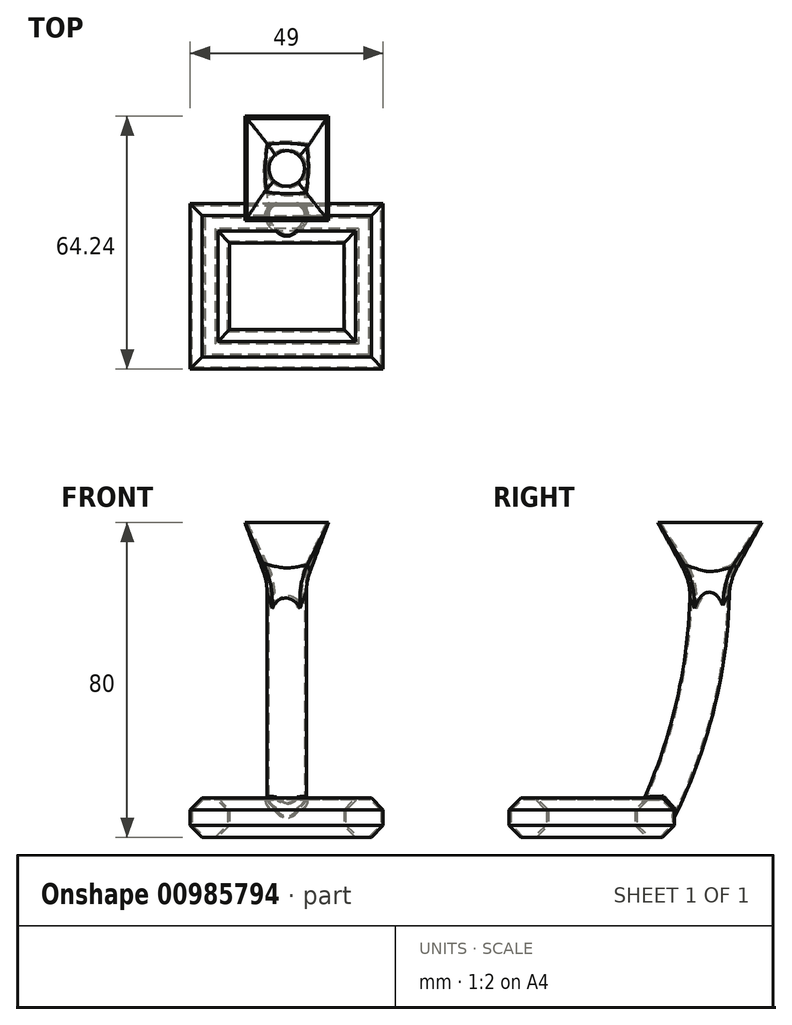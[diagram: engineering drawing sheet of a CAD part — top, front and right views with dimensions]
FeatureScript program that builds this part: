
annotation { "Feature Type Name" : "Feature", "Feature Type Description" : "" }
export const myFeature = defineFeature(function(context is Context, id is Id, definition is map)
    precondition{}
    {
        {
            assignVariable(context, id + "F0", {"variableType" : VariableType.NUMBER, "name" : "wall", "numberValue" : .5});
        }
        {
            assignVariable(context, id + "F1", {"variableType" : VariableType.LENGTH, "name" : "aird", "lengthValue" : 10 * mm});
        }
        {
            assignVariable(context, id + "F2", {"variableType" : VariableType.LENGTH, "name" : "airdr", "lengthValue" : 3 * mm});
        }
        {
            var Q0;
            Q0=qCreatedBy(makeId("Top.planeOp"),FACE);
            var sketch = newSketch(context, id + "F3", { "sketchPlane" : qUnion([Q0])});
            skLineSegment(sketch, "E0.bottom", {"start": v(11.5, 8) * mm, "end": v(-11.5, 8) * mm, "construction": true});
            skLineSegment(sketch, "E0.top", {"start": v(11.5, -8) * mm, "end": v(-11.5, -8) * mm, "construction": true});
            skLineSegment(sketch, "E0.left", {"start": v(11.5, 8) * mm, "end": v(11.5, -8) * mm, "construction": true});
            skLineSegment(sketch, "E0.right", {"start": v(-11.5, 8) * mm, "end": v(-11.5, -8) * mm, "construction": true});
            skPoint(sketch, "E0.middle", {"position": v(0, 0) * mm});
            skLineSegment(sketch, "E1.0", {"start": v(14.5, 11) * mm, "end": v(-14.5, 11) * mm});
            skLineSegment(sketch, "E1.1", {"start": v(14.5, 11) * mm, "end": v(14.5, -11) * mm});
            skLineSegment(sketch, "E1.2", {"start": v(14.5, -11) * mm, "end": v(-14.5, -11) * mm});
            skLineSegment(sketch, "E1.3", {"start": v(-14.5, 11) * mm, "end": v(-14.5, -11) * mm});
            skLineSegment(sketch, "E2.0", {"start": v(24.5, 21) * mm, "end": v(-24.5, 21) * mm});
            skLineSegment(sketch, "E2.1", {"start": v(24.5, 21) * mm, "end": v(24.5, -21) * mm});
            skLineSegment(sketch, "E2.2", {"start": v(24.5, -21) * mm, "end": v(-24.5, -21) * mm});
            skLineSegment(sketch, "E2.3", {"start": v(-24.5, 21) * mm, "end": v(-24.5, -21) * mm});
            skSolve(sketch);
        }
        {
            var Q0;
            Q0=makeQuery(id+"F3.imprint","IMPRINT",FACE,{"disambiguationData":[TD([[makeQuery(id+"F3.imprint","IMPRINT",EDGE,{"derivedFrom":sQuery(id+"F3.wireOp",EDGE,"E1.0")}),-1.0]])]});
            extrude(context, id + "F4", {"entities" : qUnion([Q0]), "depth" : getVariable(context, 'aird'), "offsetDistance" : 25 * mm});
        }
        {
            var Q0;
            Q0=makeQuery(id+"F4.opExtrude","CAP_FACE",FACE,{"disambiguationData":[OSD([sQuery(id+"F3.wireOp",EDGE,"E1.0"),sQuery(id+"F3.wireOp",EDGE,"E1.1"),sQuery(id+"F3.wireOp",EDGE,"E1.2"),sQuery(id+"F3.wireOp",EDGE,"E1.3"),sQuery(id+"F3.wireOp",EDGE,"E2.0"),sQuery(id+"F3.wireOp",EDGE,"E2.1"),sQuery(id+"F3.wireOp",EDGE,"E2.2"),sQuery(id+"F3.wireOp",EDGE,"E2.3")])],"isStart":false});
            var Q1;
            Q1=makeQuery(id+"F4.opExtrude","CAP_FACE",FACE,{"disambiguationData":[OSD([sQuery(id+"F3.wireOp",EDGE,"E1.0"),sQuery(id+"F3.wireOp",EDGE,"E1.1"),sQuery(id+"F3.wireOp",EDGE,"E1.2"),sQuery(id+"F3.wireOp",EDGE,"E1.3"),sQuery(id+"F3.wireOp",EDGE,"E2.0"),sQuery(id+"F3.wireOp",EDGE,"E2.1"),sQuery(id+"F3.wireOp",EDGE,"E2.2"),sQuery(id+"F3.wireOp",EDGE,"E2.3")])],"isStart":true});
            chamfer(context, id + "F5", {"entities" : qUnion([Q0, Q1]), "width" : getVariable(context, 'airdr'), "tangentPropagation" : true});
        }
        {
            var Q0;
            Q0=qCreatedBy(makeId("Right.planeOp"),FACE);
            var sketch = newSketch(context, id + "F6", { "sketchPlane" : qUnion([Q0])});
            skArc(sketch, "E3", {"start": v(16, 5) * mm, "mid": v(26.45, 34.2) * mm, "end": v(30, 65) * mm});
            skLineSegment(sketch, "E4", {"start": v(30, 65) * mm, "end": v(30, 55) * mm, "construction": true});
            skSolve(sketch);
        }
        {
            var Q0;
            Q0=qCreatedBy(makeId("Top.planeOp"),FACE);
            cPlane(context, id + "F7", {"entities" : qUnion([Q0]), "cplaneType" : CPlaneType.OFFSET, "offset" : 65 * mm, "width" : 150 * mm, "height" : 150 * mm});
        }
        {
            var Q0;
            Q0=qCreatedBy(id+"F7.planeOp",FACE);
            var sketch = newSketch(context, id + "F8", { "sketchPlane" : qUnion([Q0])});
            skPoint(sketch, "E5.0", {"position": v(0, 30) * mm});
            skCircle(sketch, "E6", {"center": v(0, 30) * mm, "radius": 5 * mm});
            skSolve(sketch);
        }
        {
            var Q0;
            Q0=makeQuery(id+"F8.imprint","IMPRINT",FACE,{"disambiguationData":[TD([[makeQuery(id+"F8.imprint","IMPRINT",EDGE,{"derivedFrom":sQuery(id+"F8.wireOp",EDGE,"E6")}),1.0]])]});
            var Q1;
            Q1=sQuery(id+"F6.wireOp",EDGE,"E3");
            sweep(context, id + "F9", {"operationType" : NewBodyOperationType.ADD, "profiles" : qUnion([Q0]), "path" : qUnion([Q1]), "keepProfileOrientation" : true});
        }
        {
            var Q0;
            Q0=makeQuery(id+"F9.boolean.opBoolean","INTERSECT",EDGE,{"disambiguationData":[OD(1.0)],"derivedFrom":[makeQuery(id+"F4.opExtrude","CAP_FACE",FACE,{"disambiguationData":[OSD([sQuery(id+"F3.wireOp",EDGE,"E1.0"),sQuery(id+"F3.wireOp",EDGE,"E1.1"),sQuery(id+"F3.wireOp",EDGE,"E1.2"),sQuery(id+"F3.wireOp",EDGE,"E1.3"),sQuery(id+"F3.wireOp",EDGE,"E2.0"),sQuery(id+"F3.wireOp",EDGE,"E2.1"),sQuery(id+"F3.wireOp",EDGE,"E2.2"),sQuery(id+"F3.wireOp",EDGE,"E2.3")])],"isStart":false}),makeQuery(id+"F9.opSweep","SWEPT_FACE",FACE,{"disambiguationData":[OSD([sQuery(id+"F6.wireOp",EDGE,"E3"),sQuery(id+"F8.wireOp",EDGE,"E6")])]})]});
            var Q1;
            {var subQ0=sQuery(id+"F3.wireOp",EDGE,"E1.0");Q1=makeQuery(id+"F9.boolean.opBoolean","INTERSECT",EDGE,{"derivedFrom":[makeQuery(id+"F5.opChamfer","BLEND_FACE",FACE,{"disambiguationData":[OSD([subQ0]),TDD([makeQuery(id+"F4.opExtrude","CAP_EDGE",EDGE,{"disambiguationData":[OSD([subQ0])],"isStart":false})])]}),makeQuery(id+"F9.opSweep","SWEPT_FACE",FACE,{"disambiguationData":[OSD([sQuery(id+"F6.wireOp",EDGE,"E3"),sQuery(id+"F8.wireOp",EDGE,"E6")])]})]});}
            var Q2;
            Q2=makeQuery(id+"F9.boolean.opBoolean","INTERSECT",EDGE,{"derivedFrom":[makeQuery(id+"F4.opExtrude","SWEPT_FACE",FACE,{"disambiguationData":[OSD([sQuery(id+"F3.wireOp",EDGE,"E2.0")])]}),makeQuery(id+"F9.opSweep","SWEPT_FACE",FACE,{"disambiguationData":[OSD([sQuery(id+"F6.wireOp",EDGE,"E3"),sQuery(id+"F8.wireOp",EDGE,"E6")])]})]});
            var Q3;
            {var subQ0=sQuery(id+"F3.wireOp",EDGE,"E2.0");Q3=makeQuery(id+"F9.boolean.opBoolean","INTERSECT",EDGE,{"disambiguationData":[OD(1.0)],"derivedFrom":[makeQuery(id+"F5.opChamfer","BLEND_FACE",FACE,{"disambiguationData":[OSD([subQ0]),TDD([makeQuery(id+"F4.opExtrude","CAP_EDGE",EDGE,{"disambiguationData":[OSD([subQ0])],"isStart":false})])]}),makeQuery(id+"F9.opSweep","SWEPT_FACE",FACE,{"disambiguationData":[OSD([sQuery(id+"F6.wireOp",EDGE,"E3"),sQuery(id+"F8.wireOp",EDGE,"E6")])]})]});}
            var Q4;
            Q4=makeQuery(id+"F9.boolean.opBoolean","INTERSECT",EDGE,{"disambiguationData":[OD(0.0)],"derivedFrom":[makeQuery(id+"F4.opExtrude","CAP_FACE",FACE,{"disambiguationData":[OSD([sQuery(id+"F3.wireOp",EDGE,"E1.0"),sQuery(id+"F3.wireOp",EDGE,"E1.1"),sQuery(id+"F3.wireOp",EDGE,"E1.2"),sQuery(id+"F3.wireOp",EDGE,"E1.3"),sQuery(id+"F3.wireOp",EDGE,"E2.0"),sQuery(id+"F3.wireOp",EDGE,"E2.1"),sQuery(id+"F3.wireOp",EDGE,"E2.2"),sQuery(id+"F3.wireOp",EDGE,"E2.3")])],"isStart":false}),makeQuery(id+"F9.opSweep","SWEPT_FACE",FACE,{"disambiguationData":[OSD([sQuery(id+"F6.wireOp",EDGE,"E3"),sQuery(id+"F8.wireOp",EDGE,"E6")])]})]});
            var Q5;
            {var subQ0=sQuery(id+"F3.wireOp",EDGE,"E2.0");Q5=makeQuery(id+"F9.boolean.opBoolean","INTERSECT",EDGE,{"disambiguationData":[OD(0.0)],"derivedFrom":[makeQuery(id+"F5.opChamfer","BLEND_FACE",FACE,{"disambiguationData":[OSD([subQ0]),TDD([makeQuery(id+"F4.opExtrude","CAP_EDGE",EDGE,{"disambiguationData":[OSD([subQ0])],"isStart":false})])]}),makeQuery(id+"F9.opSweep","SWEPT_FACE",FACE,{"disambiguationData":[OSD([sQuery(id+"F6.wireOp",EDGE,"E3"),sQuery(id+"F8.wireOp",EDGE,"E6")])]})]});}
            fillet(context, id + "F10", {"entities" : qUnion([Q0, Q1, Q2, Q3, Q4, Q5]), "tangentPropagation" : true, "radius" : .5 * mm, "defaultsChanged" : true, "vertexSettings" : [], "allowEdgeOverflow" : false});
        }
        {
            var Q0;
            Q0=qCreatedBy(makeId("Top.planeOp"),FACE);
            cPlane(context, id + "F11", {"entities" : qUnion([Q0]), "cplaneType" : CPlaneType.OFFSET, "offset" : 80 * mm, "width" : 150 * mm, "height" : 150 * mm});
        }
        {
            var Q0;
            Q0=qCreatedBy(id+"F11.planeOp",FACE);
            var sketch = newSketch(context, id + "F12", { "sketchPlane" : qUnion([Q0])});
            skPoint(sketch, "E7.0", {"position": v(0, 30) * mm});
            skLineSegment(sketch, "E8.bottom", {"start": v(10.63, 16.76) * mm, "end": v(-10.63, 16.76) * mm});
            skLineSegment(sketch, "E8.top", {"start": v(10.63, 43.24) * mm, "end": v(-10.63, 43.24) * mm});
            skLineSegment(sketch, "E8.left", {"start": v(10.63, 16.76) * mm, "end": v(10.63, 43.24) * mm});
            skLineSegment(sketch, "E8.right", {"start": v(-10.63, 16.76) * mm, "end": v(-10.63, 43.24) * mm});
            skSolve(sketch);
        }
        {
            var Q0;
            Q0=makeQuery(id+"F12.imprint","IMPRINT",FACE,{"disambiguationData":[TD([[makeQuery(id+"F12.imprint","IMPRINT",EDGE,{"derivedFrom":sQuery(id+"F12.wireOp",EDGE,"E8.bottom")}),-1.0]])]});
            var Q1;
            Q1=makeQuery(id+"F8.imprint","IMPRINT",FACE,{"disambiguationData":[TD([[makeQuery(id+"F8.imprint","IMPRINT",EDGE,{"derivedFrom":sQuery(id+"F8.wireOp",EDGE,"E6")}),1.0]])]});
            loft(context, id + "F13", {"operationType" : NewBodyOperationType.ADD, "sheetProfilesArray" : [{ "sheetProfileEntities" : qUnion([Q0]) }, { "sheetProfileEntities" : qUnion([Q1]) }]});
        }
        {
            var Q0;
            {var subQ0=sQuery(id+"F8.wireOp",EDGE,"E6");Q0=makeQuery(id+"F13.boolean.opBoolean","MERGE",EDGE,{"derivedFrom":[makeQuery(id+"F9.opSweep","CAP_EDGE",EDGE,{"disambiguationData":[OSD([sQuery(id+"F6.wireOp",VERTEX,"E3.end"),subQ0])],"isStart":true}),makeQuery(id+"F13.opLoft","MID_CAP_EDGE",EDGE,{"disambiguationData":[OSD([subQ0,sQuery(id+"F12.wireOp",EDGE,"E8.bottom"),sQuery(id+"F12.wireOp",EDGE,"E8.left")])],"capPos":1.0})]});}
            var Q1;
            {var subQ0=sQuery(id+"F8.wireOp",EDGE,"E6");Q1=makeQuery(id+"F13.boolean.opBoolean","MERGE",EDGE,{"derivedFrom":[makeQuery(id+"F9.opSweep","CAP_EDGE",EDGE,{"disambiguationData":[OSD([sQuery(id+"F6.wireOp",VERTEX,"E3.end"),subQ0])],"isStart":true}),makeQuery(id+"F13.opLoft","MID_CAP_EDGE",EDGE,{"disambiguationData":[OSD([subQ0,sQuery(id+"F12.wireOp",EDGE,"E8.bottom"),sQuery(id+"F12.wireOp",EDGE,"E8.left"),sQuery(id+"F12.wireOp",EDGE,"E8.right")])],"capPos":1.0})]});}
            var Q2;
            {var subQ0=sQuery(id+"F8.wireOp",EDGE,"E6");Q2=makeQuery(id+"F13.boolean.opBoolean","MERGE",EDGE,{"derivedFrom":[makeQuery(id+"F9.opSweep","CAP_EDGE",EDGE,{"disambiguationData":[OSD([sQuery(id+"F6.wireOp",VERTEX,"E3.end"),subQ0])],"isStart":true}),makeQuery(id+"F13.opLoft","MID_CAP_EDGE",EDGE,{"disambiguationData":[OSD([subQ0,sQuery(id+"F12.wireOp",EDGE,"E8.bottom"),sQuery(id+"F12.wireOp",EDGE,"E8.top"),sQuery(id+"F12.wireOp",EDGE,"E8.right")])],"capPos":1.0})]});}
            var Q3;
            {var subQ0=sQuery(id+"F8.wireOp",EDGE,"E6");Q3=makeQuery(id+"F13.boolean.opBoolean","MERGE",EDGE,{"derivedFrom":[makeQuery(id+"F9.opSweep","CAP_EDGE",EDGE,{"disambiguationData":[OSD([sQuery(id+"F6.wireOp",VERTEX,"E3.end"),subQ0])],"isStart":true}),makeQuery(id+"F13.opLoft","MID_CAP_EDGE",EDGE,{"disambiguationData":[OSD([subQ0,sQuery(id+"F12.wireOp",EDGE,"E8.bottom"),sQuery(id+"F12.wireOp",EDGE,"E8.top"),sQuery(id+"F12.wireOp",EDGE,"E8.left"),sQuery(id+"F12.wireOp",EDGE,"E8.right")])],"capPos":1.0})]});}
            fillet(context, id + "F14", {"entities" : qUnion([Q0, Q1, Q2, Q3]), "tangentPropagation" : true, "radius" : 15 * mm, "defaultsChanged" : true, "vertexSettings" : [], "allowEdgeOverflow" : false});
        }
        {
            var Q0;
            Q0=makeQuery(id+"F13.opLoft","CAP_FACE",FACE,{"disambiguationData":[OSD([makeQuery(id+"F12.imprint","IMPRINT",FACE,{"disambiguationData":[TD([[makeQuery(id+"F12.imprint","IMPRINT",EDGE,{"derivedFrom":sQuery(id+"F12.wireOp",EDGE,"E8.bottom")}),-1.0]])]})])],"isStart":true});
            var Q1;
            Q1=makeQuery(id+"F4.opExtrude","CAP_FACE",FACE,{"disambiguationData":[OSD([sQuery(id+"F3.wireOp",EDGE,"E1.0"),sQuery(id+"F3.wireOp",EDGE,"E1.1"),sQuery(id+"F3.wireOp",EDGE,"E1.2"),sQuery(id+"F3.wireOp",EDGE,"E1.3"),sQuery(id+"F3.wireOp",EDGE,"E2.0"),sQuery(id+"F3.wireOp",EDGE,"E2.1"),sQuery(id+"F3.wireOp",EDGE,"E2.2"),sQuery(id+"F3.wireOp",EDGE,"E2.3")])],"isStart":true});
            shell(context, id + "F15", {"entities" : qUnion([Q0, Q1]), "thickness" : (getVariable(context, 'wall')) * mm});
        }
    });
